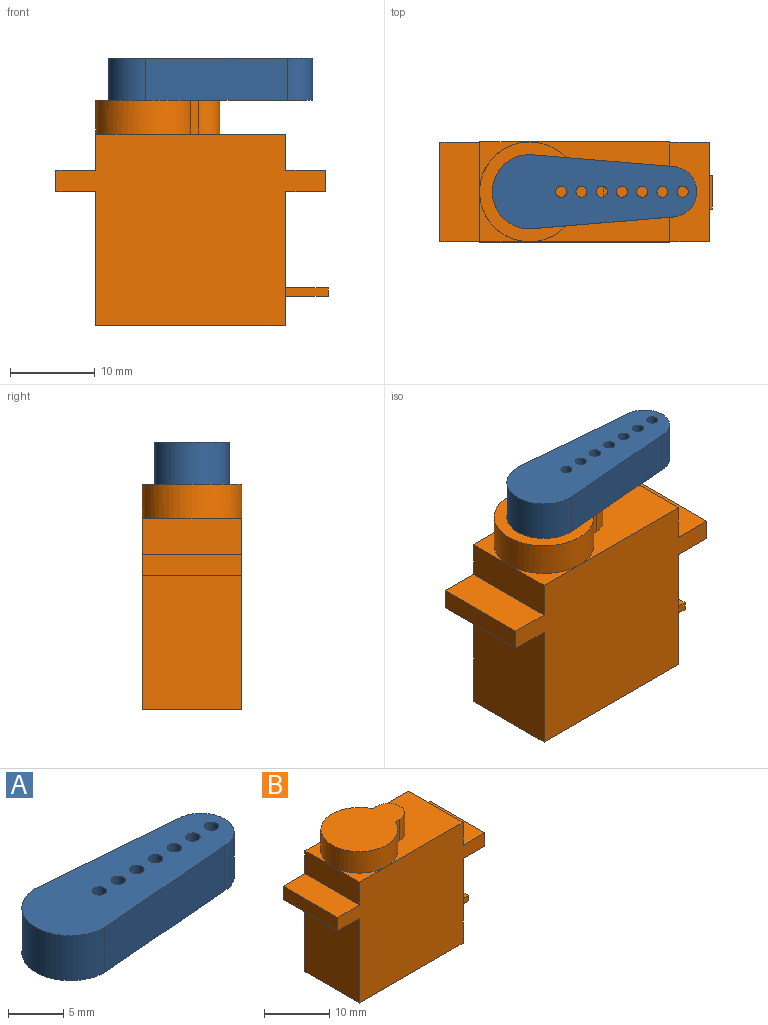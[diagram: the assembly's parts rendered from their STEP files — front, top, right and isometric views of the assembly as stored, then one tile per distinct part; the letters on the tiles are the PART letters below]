
ASSEMBLY  parts=2 mates=1
PART A: 13 faces, bbox 24.2x8.8x5 mm
  f0: plane 16.78x5mm, normal (0.08,-1,0), area 84.2mm2, adj f1,f9,f11,f12
  f1: cylinder r=3mm len=6mm, axis (0,0,-1), area 47.1mm2, adj f0,f2,f11,f12
  f2: plane 16.78x5mm, normal (0.08,1,0), area 84.2mm2, adj f1,f9,f11,f12
  f3: cylinder r=0.65mm len=5mm, axis (0,0,-1), area 20.5mm2, adj f11,f12
  f4: cylinder r=0.65mm len=5mm, axis (0,0,-1), area 20.5mm2, adj f11,f12
  f5: cylinder r=0.65mm len=5mm, axis (0,0,-1), area 20.5mm2, adj f11,f12
  f6: cylinder r=0.65mm len=5mm, axis (0,0,-1), area 20.5mm2, adj f11,f12
  f7: cylinder r=0.65mm len=5mm, axis (0,0,-1), area 20.5mm2, adj f11,f12
  f8: cylinder r=0.65mm len=5mm, axis (0,0,-1), area 20.5mm2, adj f11,f12
  f9: cylinder r=4.4mm len=8.8mm, axis (0,0,-1), area 69.1mm2, adj f0,f2,f11,f12
  f10: cylinder r=0.65mm len=5mm, axis (0,0,-1), area 20.5mm2, adj f11,f12
  f11: plane 24.18x8.8mm, normal (0,0,1), area 159.4mm2, adj f0,f1,f2,f3,f4,f5,f6,f7
  f12: plane 24.18x8.8mm, normal (0,0,-1), area 159.4mm2, adj f0,f1,f2,f3,f4,f5,f6,f7
PART B: 26 faces, bbox 32.2x11.8x26.7 mm
  f0: plane 16.6x11.8mm, normal (0,0,1), area 128.5mm2, adj f12,f14,f15,f16,f17,f18,f19
  f1: plane 5.9x5.9mm, normal (0,0,1), area 7.5mm2, adj f2,f14,f17
  f2: plane 11.8x4.3mm, normal (-1,0,0), area 50.7mm2, adj f1,f3,f13,f14,f15
  f3: plane 11.8x4.7mm, normal (0,0,1), area 55.5mm2, adj f2,f4,f14,f15
  f4: plane 11.8x2.5mm, normal (-1,0,0), area 29.5mm2, adj f3,f5,f14,f15
  f5: plane 11.8x4.7mm, normal (0,0,-1), area 55.5mm2, adj f4,f6,f14,f15
  f6: plane 15.9x11.8mm, normal (-1,0,0), area 187.6mm2, adj f5,f7,f14,f15
  f7: plane 22.5x11.8mm, normal (0,0,-1), area 265.5mm2, adj f6,f8,f14,f15
  f8: plane 15.9x11.8mm, normal (1,0,0), area 183.6mm2, adj f7,f9,f14,f15,f21,f22,f23,f24
  f9: plane 11.8x4.7mm, normal (0,0,-1), area 55.5mm2, adj f8,f10,f14,f15
  f10: plane 11.8x2.5mm, normal (1,0,0), area 29.5mm2, adj f9,f11,f14,f15
  f11: plane 11.8x4.7mm, normal (0,0,1), area 55.5mm2, adj f10,f12,f14,f15
  f12: plane 11.8x4.3mm, normal (1,0,0), area 50.7mm2, adj f0,f11,f14,f15
  f13: plane 5.9x5.9mm, normal (0,0,1), area 7.5mm2, adj f2,f15,f17
  f14: plane 31.9x22.7mm, normal (0,1,0), area 534.2mm2, adj f0,f1,f2,f3,f4,f5,f6,f7
  f15: plane 31.9x22.7mm, normal (0,-1,0), area 534.2mm2, adj f0,f2,f3,f4,f5,f6,f7,f8
  f16: plane 4x0.96mm, normal (0,1,0), area 3.8mm2, adj f0,f17,f19,f20
  f17: cylinder r=5.9mm len=11.8mm, axis (0,0,-1), area 127.6mm2, adj f0,f1,f13,f16,f18,f20
  f18: plane 4x0.96mm, normal (0,-1,0), area 3.8mm2, adj f0,f17,f19,f20
  f19: cylinder r=2.5mm len=5mm, axis (0,0,-1), area 31.4mm2, adj f0,f16,f18,f20
  f20: plane 14.7x11.8mm, normal (0,0,1), area 122.1mm2, adj f16,f17,f18,f19
  f21: plane 5x1mm, normal (0,1,0), area 5mm2, adj f8,f22,f24,f25
  f22: plane 5x4mm, normal (0,0,1), area 20mm2, adj f8,f21,f23,f25
  f23: plane 5x1mm, normal (0,-1,0), area 5mm2, adj f8,f22,f24,f25
  f24: plane 5x4mm, normal (0,0,-1), area 20mm2, adj f8,f21,f23,f25
  f25: plane 4x1mm, normal (1,0,0), area 4mm2, adj f21,f22,f23,f24
PLACE A t=(-27.21,-4.46,-1.42)mm
PLACE B t=(-27.21,-4.46,-1.42)mm
MATE revolute A.f9 <-> B.f17  axis (0,0,-1) through (-22.36,1.44,27.54)mm
